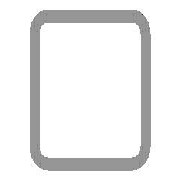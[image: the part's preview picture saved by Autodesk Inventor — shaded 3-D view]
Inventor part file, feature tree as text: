
AUTODESK INVENTOR PART (.ipt)
format: ipt  version: 2024.2 (Build 282272000, 272)  size: 126,976 bytes
history: native  units: mm (DEFAULTED — no unit token found)
features: other x4, sketch x1, plane x1
ambient origin geometry x8: Origin, YZ Plane, XZ Plane, XY Plane, X Axis, Y Axis, Z Axis, Center Point
bodies: Solid1 (feature_tree), Body (feature_tree)
feature tree (6):
  parser-record x1  (decoder bookkeeping rows leaked as tree rows — omitted from the tree; the rows remain in map.json)
  other  "Driven Length"
  other  "Start Plane"
  other  "End Plane"
  sketch  "Sketch3"  dims[d3=2250.0mm d4=0.0mm d7=6.0mm d9=50.0mm d11=50.0mm d12=3.0mm d13=-0.0mm d14=2250.0mm d15=25.0mm d16=25.0mm d17=90.0deg d18=2250.0mm]
  plane  "Work Plane3"
